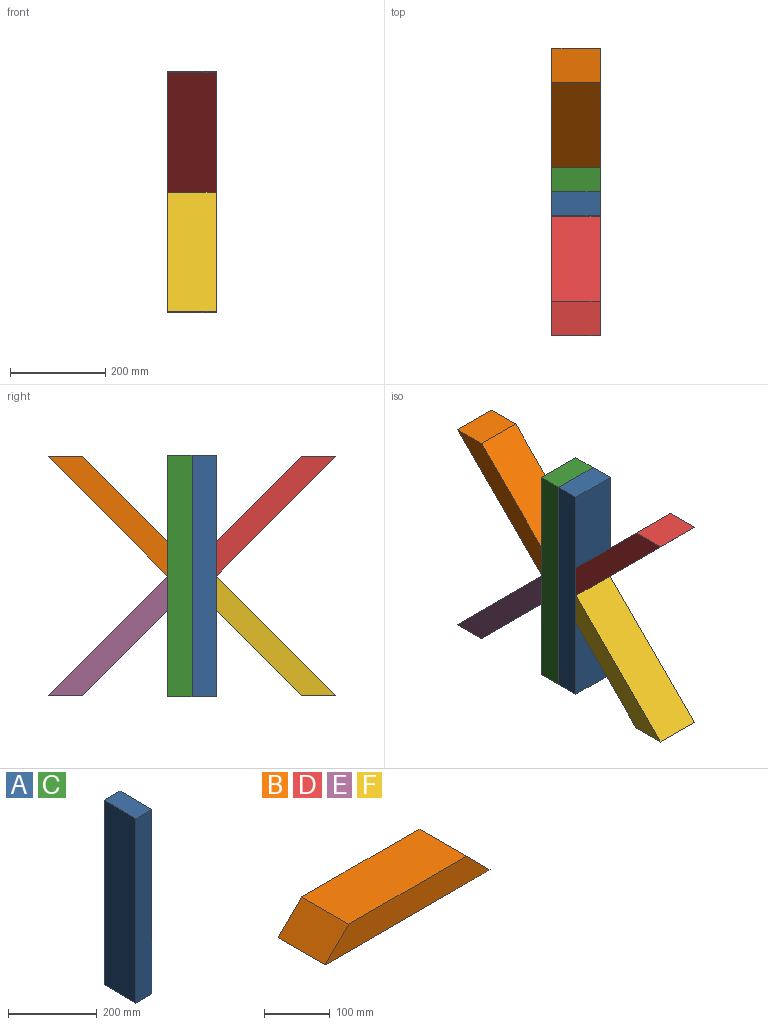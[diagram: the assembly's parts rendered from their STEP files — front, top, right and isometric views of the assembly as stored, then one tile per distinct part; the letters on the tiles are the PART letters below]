
ASSEMBLY  parts=6 mates=8
PART A: 6 faces, bbox 50.8x101.6x508 mm
  f0: plane 508x101.6mm, normal (-1,0,0), area 51612.8mm2, adj f1,f3,f4,f5
  f1: plane 101.6x50.8mm, normal (0,0,-1), area 5161.3mm2, adj f0,f2,f4,f5
  f2: plane 508x101.6mm, normal (1,0,0), area 51612.8mm2, adj f1,f3,f4,f5
  f3: plane 101.6x50.8mm, normal (0,0,1), area 5161.3mm2, adj f0,f2,f4,f5
  f4: plane 508x50.8mm, normal (0,-1,0), area 25806.4mm2, adj f0,f1,f2,f3
  f5: plane 508x50.8mm, normal (0,1,0), area 25806.4mm2, adj f0,f1,f2,f3
PART B: 6 faces, bbox 355.6x101.6x50.8 mm
  f0: plane 254x101.6mm, normal (0,0,1), area 25806.4mm2, adj f1,f3,f4,f5
  f1: plane 101.6x50.8mm, normal (-0.71,0,0.71), area 7299.2mm2, adj f0,f2,f4,f5
  f2: plane 355.6x101.6mm, normal (0,0,-1), area 36129mm2, adj f1,f3,f4,f5
  f3: plane 101.6x50.8mm, normal (0.71,0,0.71), area 7299.2mm2, adj f0,f2,f4,f5
  f4: plane 355.6x50.8mm, normal (0,-1,0), area 15483.8mm2, adj f0,f1,f2,f3
  f5: plane 355.6x50.8mm, normal (0,1,0), area 15483.8mm2, adj f0,f1,f2,f3
PART C: same geometry as A
PART D: same geometry as B
PART E: same geometry as B
PART F: same geometry as B
PLACE A rot(axis=(0,0,1),90deg) t=(0,-25.4,0)mm
PLACE B rot(axis=(0.36,-0.36,0.86),98.4deg) t=(0.29,406.7,408.03)mm
PLACE C rot(axis=(0,0,-1),90deg) t=(0,25.4,0)mm
PLACE D rot(axis=(-0.36,-0.36,-0.86),98.4deg) t=(-0.05,-406.7,408.15)mm
PLACE E rot(axis=(0.68,0.68,-0.28),148.6deg) t=(0.29,406.7,-408.35)mm
PLACE F rot(axis=(-0.68,-0.68,-0.28),148.6deg) t=(-0.05,105.94,104.4)mm
MATE planar B.f1 <-> C.f0  axis (0,-1,0) through (0.29,50.8,-0.16)mm
MATE planar A.f2 <-> C.f2  axis (0,1,0) through (0,0,0)mm
MATE planar B.f1 <-> E.f1  axis (0,-1,0) through (0.29,50.8,-0.16)mm
MATE planar C.f0 <-> E.f1  axis (0,1,0) through (0,50.8,0)mm
MATE planar E.f1 <-> C.f0  axis (0,-1,0) through (0.29,50.8,-0.16)mm
MATE planar B.f1 <-> E.f1  axis (0,-1,0) through (0.29,50.8,-0.16)mm
MATE planar D.f1 <-> F.f3  axis (0,1,0) through (-0.05,-50.8,-0.04)mm
MATE planar D.f1 <-> A.f0  axis (0,1,0) through (-0.05,-50.8,-0.04)mm
